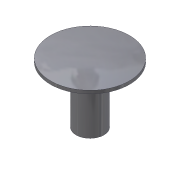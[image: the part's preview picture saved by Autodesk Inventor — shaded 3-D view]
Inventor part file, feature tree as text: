
AUTODESK INVENTOR PART (.ipt)
format: ipt  version: 2014 (Build 180170000, 170)  size: 91,136 bytes
history: native  units: mm (DEFAULTED — no unit token found)
features: sketch x2, reference x2, revolve x1, extrude x1
ambient origin geometry x8: Origin, YZ Plane, XZ Plane, XY Plane, X Axis, Y Axis, Z Axis, Center Point
bodies: Solid1 (feature_tree)
feature tree (6):
  revolve  "Revolution1"  [1 undecoded]
  extrude  "Extrusion1"  [1 undecoded]
  sketch  "Sketch1"  dims[d0=90.0deg d1=3.175mm d2=0.0mm]
  reference  "Reference1"
  reference  "Reference2"
  sketch  "Sketch2"
note: 2 required parameter values undecoded (feature->parameter linkage not recoverable at this tier; creation-order binding heuristic only, values carry confidence <= 0.55)